# Revit family: Vitra-Sento-Illuminated Mirror Cabinet-60893-61666-61667-61668-60892-61669-61670-61671
name_source: partatom
category: Casework
units: mm (PartAtom-declared; Revit-internal decimal feet)

## family parameters
Cut with Voids When Loaded = No
Host = Face
OmniClass Number = 23.40.35.00
OmniClass Title = Casework
Room Calculation Point = No
Shared = Yes

## types (8) — shared parameters
BIMobject category = Storage
Construction Type = Wall Mounted
Default Elevation = 1250 mm  [stored 4.10105 ft]
Depth = 150 mm
Description = Sento Illuminated Mirror Cabinet, 50 cm
Design country = Turkey
Height = 700 mm  [stored 2.29659 ft]
IFC Classification = Furnishing Element
Installation instructions = https://cdn.vitra.com.tr
Light = Vitra-Light
Manufacturer = Vitra
Manufacturer name = Vitra
Masterformat 2014 Code = 41 53 13
Masterformat 2014 Description = Storage Cabinets
NBS Reference Code = 35-75-08
NBS Reference Description = Bathroom Cabinets
OmniClass Code = 23-25 53 11 13 11
OmniClass Description = Medicine Cabinets
Product Guid = https://cdn.vitra.com.tr
Product certification = https://vitraglobal.com
Product data url = https://www.vitraglobal.com
Product family = Sento
Product group = Bathroom Furniture
Secondary Material = Vitra-Mirror
Technical description = https://www.vitraglobal.com
UNSPSC Code = 30161801
UNSPSC Description = Bathroom cabinets
URL = https://vitraglobal.com
Uniclass 1.4 Code = L72141
Uniclass 1.4 Description = Cabinets
Uniclass 2.0 Code = PR-35-75-08
Uniclass 2.0 Description = Bathroom Cabinets
Uniclass 2015 Code = Pr_40_30_78_03
Uniclass 2015 Name = Bathroom cabinets
Uniformat II Code = E20
Uniformat II Description = Furnishings
Voltage = 220V
Warranty Period (Year) = 2
Weight Net (kg) = 18,500
Width = 500 mm  [stored 1.64042 ft]
Youtube = https://www.youtube.com
zero-valued in all types: Nominal height, Nominal width

## per-type parameters (varying)
| type | Material main | Model | Product SKU |
| Vitra_Sento_Illuminated Mirror Cabinet, 50 cm, MLight Oak_Left_60893 | Vitra-Wood-Light Oak | 60893 | 60893 |
| Vitra_Sento_Illuminated Mirror Cabinet, 50 cm, Matte White_Left_61666 | Vitra-Wood-Matt White | 61666 | 61666 |
| Vitra_Sento_Illuminated Mirror Cabinet, 50 cm, Matte Cream_Left_61667 | Vitra-Wood-Matte Cream | 61667 | 61667 |
| Vitra_Sento_Illuminated Mirror Cabinet, 50 cm, Matte Anthracite_Left_61668 | Vitra-Wood-Dark Olive | 61668 | 61668 |
| Vitra_Sento_Illuminated Mirror Cabinet, 50 cm, MLight Oak_Right_60892 | Vitra-Wood-Light Oak | 60892 | 60892 |
| Vitra_Sento_Illuminated Mirror Cabinet, 50 cm, Matte White_Right_61669 | Vitra-Wood-Matt White | 61669 | 61669 |
| Vitra_Sento_Illuminated Mirror Cabinet, 50 cm, Matte Cream_Right_61670 | Vitra-Wood-Matte Cream | 61670 | 61670 |
| Vitra_Sento_Illuminated Mirror Cabinet, 50 cm, Matte Anthracite_Right_61671 | Vitra-Wood-Dark Olive | 61671 | 61671 |

note: [stored X ft] marks values corroborated as IEEE doubles in the binary element streams (Revit-internal decimal feet)

## geometry (parser evidence)
native form markers: Sweep x3
no freeform markers — native parametric forms only
